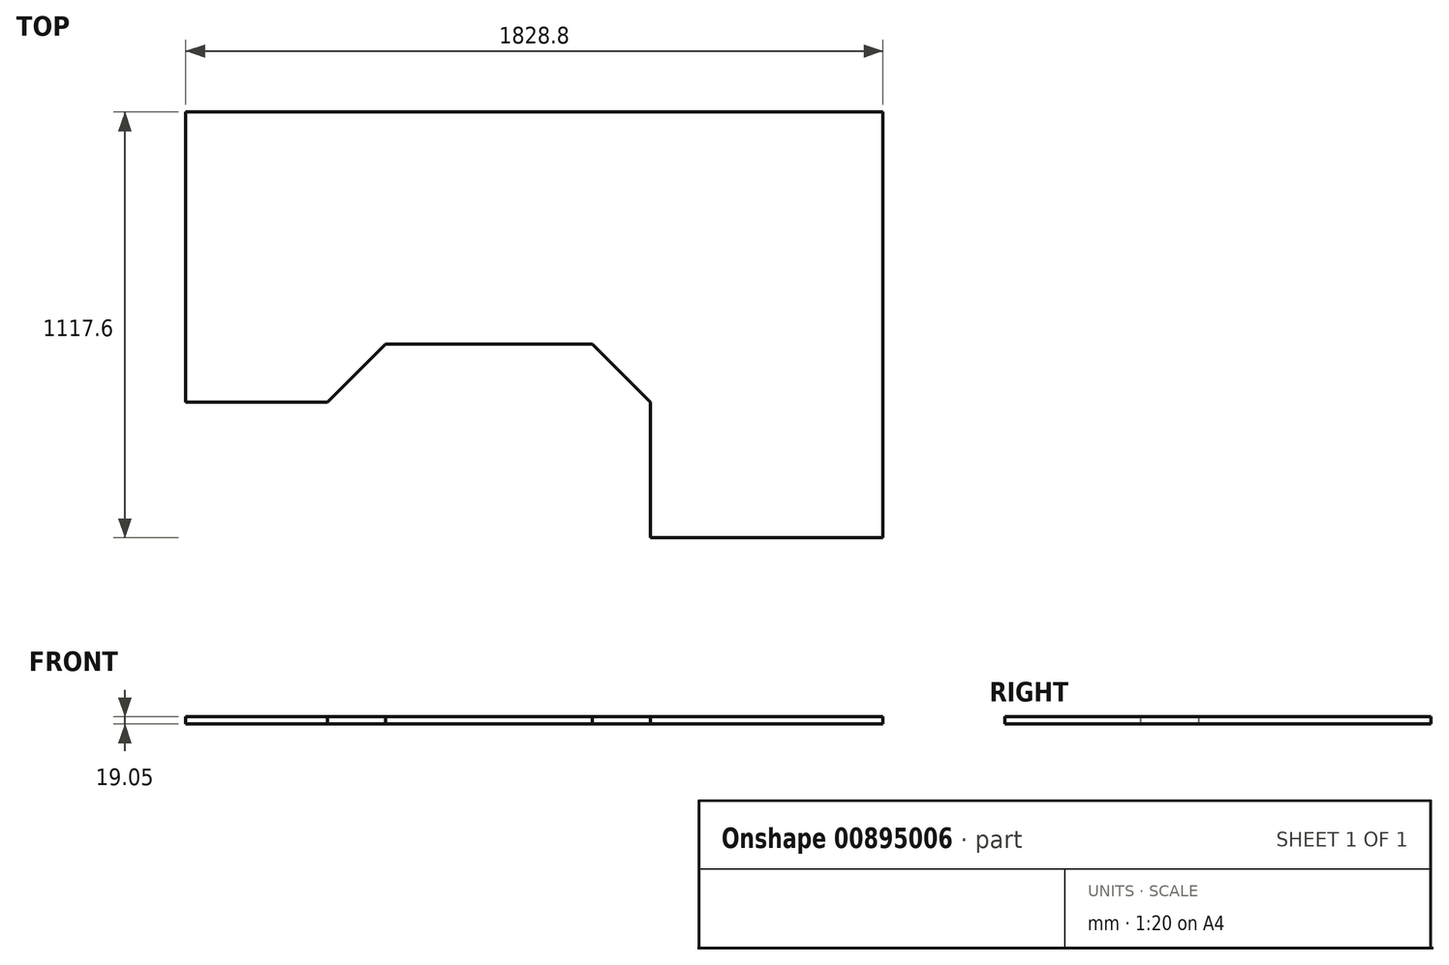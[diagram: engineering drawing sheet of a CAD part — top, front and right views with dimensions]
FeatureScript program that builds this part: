
annotation { "Feature Type Name" : "Feature", "Feature Type Description" : "" }
export const myFeature = defineFeature(function(context is Context, id is Id, definition is map)
    precondition{}
    {
        {
            var Q0;
            Q0=qCreatedBy(makeId("Top.planeOp"),FACE);
            var sketch = newSketch(context, id + "F0", { "sketchPlane" : qUnion([Q0])});
            skLineSegment(sketch, "E0.bottom", {"start": v(609.6, 609.6) * mm, "end": v(-1219.2, 609.6) * mm});
            skLineSegment(sketch, "E0.top", {"start": v(609.6, -508) * mm, "end": v(0, -508) * mm});
            skLineSegment(sketch, "E0.left", {"start": v(609.6, 609.6) * mm, "end": v(609.6, -508) * mm});
            skLineSegment(sketch, "E0.right", {"start": v(-1219.2, 609.6) * mm, "end": v(-1219.2, -152.4) * mm});
            skLineSegment(sketch, "E1.top", {"start": v(-1219.2, -152.4) * mm, "end": v(-847.73, -152.4) * mm});
            skLineSegment(sketch, "E2", {"start": v(-847.73, -152.4) * mm, "end": v(-695.33, 0) * mm});
            skLineSegment(sketch, "E3", {"start": v(-695.33, 0) * mm, "end": v(-152.4, 0) * mm});
            skLineSegment(sketch, "E4", {"start": v(0, -152.4) * mm, "end": v(0, -508) * mm});
            skLineSegment(sketch, "E5", {"start": v(-152.4, 0) * mm, "end": v(0, -152.4) * mm});
            skPoint(sketch, "E6.orphan", {"position": v(0, 0) * mm});
            skSolve(sketch);
        }
        {
            var Q0;
            Q0=makeQuery(id+"F0.imprint","IMPRINT",FACE,{"disambiguationData":[TD([[makeQuery(id+"F0.imprint","IMPRINT",EDGE,{"derivedFrom":sQuery(id+"F0.wireOp",EDGE,"E0.bottom")}),1.0]])]});
            extrude(context, id + "F1", {"entities" : qUnion([Q0]), "depth" : 19.05 * mm, "offsetDistance" : 25.4 * mm});
        }
    });
